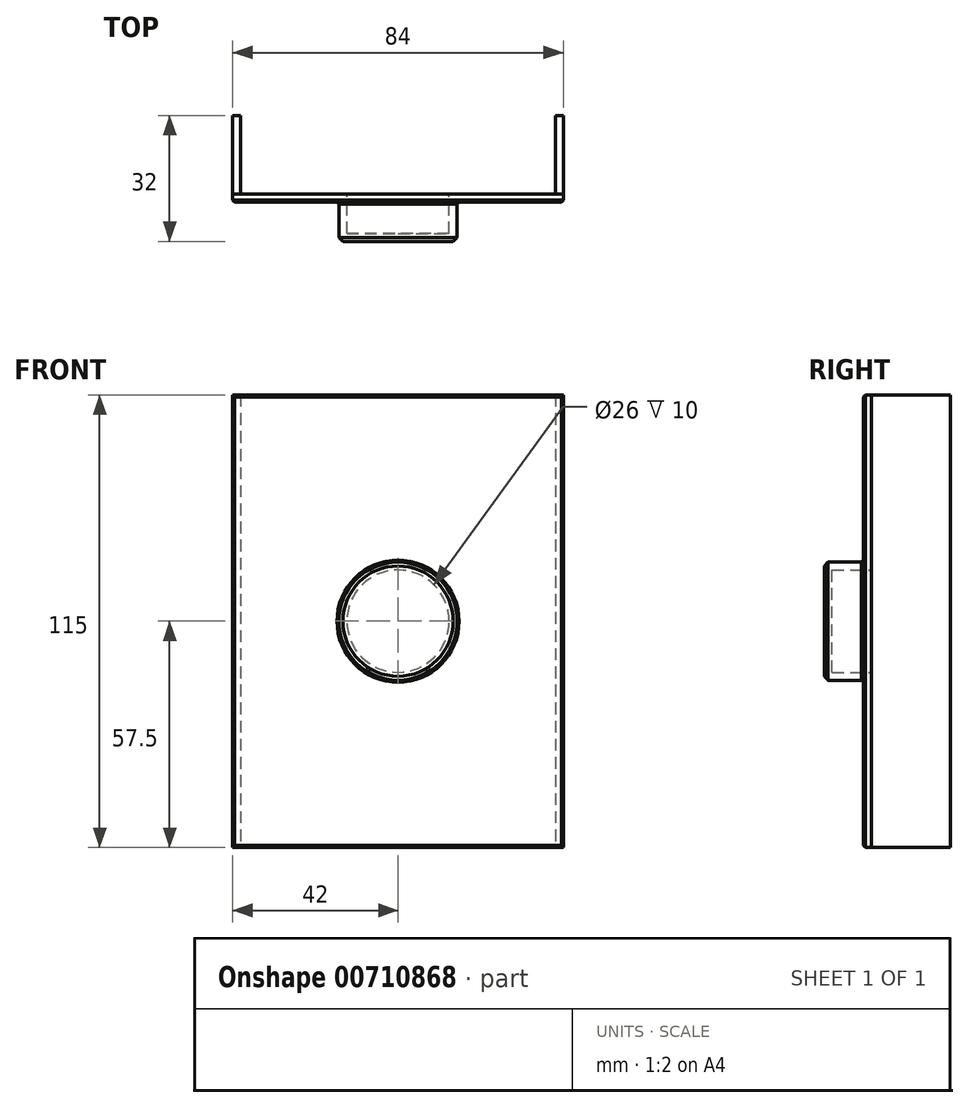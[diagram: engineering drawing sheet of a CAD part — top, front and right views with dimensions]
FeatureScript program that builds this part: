
annotation { "Feature Type Name" : "Feature", "Feature Type Description" : "" }
export const myFeature = defineFeature(function(context is Context, id is Id, definition is map)
    precondition{}
    {
        {
            var Q0;
            Q0=qCreatedBy(makeId("Front.planeOp"),FACE);
            var sketch = newSketch(context, id + "F0", { "sketchPlane" : qUnion([Q0])});
            skLineSegment(sketch, "E0.bottom", {"start": v(-40, 57.5) * mm, "end": v(40, 57.5) * mm});
            skLineSegment(sketch, "E0.top", {"start": v(-40, -57.5) * mm, "end": v(40, -57.5) * mm});
            skLineSegment(sketch, "E0.left", {"start": v(-40, 57.5) * mm, "end": v(-40, -57.5) * mm});
            skLineSegment(sketch, "E0.right", {"start": v(40, 57.5) * mm, "end": v(40, -57.5) * mm});
            skLineSegment(sketch, "E1.bottom", {"start": v(-40, 57.5) * mm, "end": v(-42, 57.5) * mm});
            skLineSegment(sketch, "E1.top", {"start": v(-40, -57.5) * mm, "end": v(-42, -57.5) * mm});
            skLineSegment(sketch, "E1.right", {"start": v(-42, 57.5) * mm, "end": v(-42, -57.5) * mm});
            skLineSegment(sketch, "E2.bottom", {"start": v(40, 57.5) * mm, "end": v(42, 57.5) * mm});
            skLineSegment(sketch, "E2.top", {"start": v(40, -57.5) * mm, "end": v(42, -57.5) * mm});
            skLineSegment(sketch, "E2.right", {"start": v(42, 57.5) * mm, "end": v(42, -57.5) * mm});
            skCircle(sketch, "E3", {"center": v(0, 0) * mm, "radius": 13 * mm});
            skCircle(sketch, "E4", {"center": v(0, 0) * mm, "radius": 15 * mm});
            skSolve(sketch);
        }
        {
            var Q0;
            Q0=makeQuery(id+"F0.imprint","IMPRINT",FACE,{"disambiguationData":[TD([[makeQuery(id+"F0.imprint","IMPRINT",EDGE,{"derivedFrom":sQuery(id+"F0.wireOp",EDGE,"E1.bottom")}),1.0]])]});
            extrude(context, id + "F1", {"entities" : qUnion([Q0]), "oppositeDirection" : true, "depth" : 20 * mm, "offsetDistance" : 25 * mm});
        }
        {
            var Q0;
            Q0=makeQuery(id+"F0.imprint","IMPRINT",FACE,{"disambiguationData":[TD([[makeQuery(id+"F0.imprint","IMPRINT",EDGE,{"derivedFrom":sQuery(id+"F0.wireOp",EDGE,"E2.bottom")}),-1.0]])]});
            extrude(context, id + "F2", {"entities" : qUnion([Q0]), "oppositeDirection" : true, "depth" : 20 * mm, "offsetDistance" : 25 * mm});
        }
        {
            var Q0;
            Q0=makeQuery(id+"F0.imprint","IMPRINT",FACE,{"disambiguationData":[TD([[makeQuery(id+"F0.imprint","IMPRINT",EDGE,{"derivedFrom":sQuery(id+"F0.wireOp",EDGE,"E0.bottom")}),-1.0]])]});
            var Q1;
            Q1=makeQuery(id+"F0.imprint","IMPRINT",FACE,{"disambiguationData":[TD([[makeQuery(id+"F0.imprint","IMPRINT",EDGE,{"derivedFrom":sQuery(id+"F0.wireOp",EDGE,"E2.bottom")}),-1.0]])]});
            var Q2;
            Q2=makeQuery(id+"F0.imprint","IMPRINT",FACE,{"disambiguationData":[TD([[makeQuery(id+"F0.imprint","IMPRINT",EDGE,{"derivedFrom":sQuery(id+"F0.wireOp",EDGE,"E1.bottom")}),1.0]])]});
            extrude(context, id + "F3", {"entities" : qUnion([Q0, Q1, Q2]), "depth" : 2 * mm, "offsetDistance" : 25 * mm});
        }
        {
            var Q0;
            Q0=makeQuery(id+"F0.imprint","IMPRINT",FACE,{"disambiguationData":[TD([[makeQuery(id+"F0.imprint","IMPRINT",EDGE,{"derivedFrom":sQuery(id+"F0.wireOp",EDGE,"E3")}),-1.0]])]});
            var Q1;
            Q1=makeQuery(id+"F0.imprint","IMPRINT",FACE,{"disambiguationData":[TD([[makeQuery(id+"F0.imprint","IMPRINT",EDGE,{"derivedFrom":sQuery(id+"F0.wireOp",EDGE,"E3")}),1.0]])]});
            extrude(context, id + "F4", {"entities" : qUnion([Q0, Q1]), "operationType" : NewBodyOperationType.ADD, "depth" : 12 * mm, "offsetDistance" : 25 * mm});
        }
        {
            var Q0;
            Q0=makeQuery(id+"F0.imprint","IMPRINT",FACE,{"disambiguationData":[TD([[makeQuery(id+"F0.imprint","IMPRINT",EDGE,{"derivedFrom":sQuery(id+"F0.wireOp",EDGE,"E3")}),1.0]])]});
            extrude(context, id + "F5", {"entities" : qUnion([Q0]), "operationType" : NewBodyOperationType.REMOVE, "depth" : 10 * mm, "offsetDistance" : 25 * mm});
        }
        {
            var Q0;
            Q0=makeQuery(id+"F3.opExtrude","CAP_FACE",FACE,{"disambiguationData":[OSD([sQuery(id+"F0.wireOp",EDGE,"E0.bottom"),sQuery(id+"F0.wireOp",EDGE,"E0.top"),sQuery(id+"F0.wireOp",EDGE,"E1.bottom"),sQuery(id+"F0.wireOp",EDGE,"E1.top"),sQuery(id+"F0.wireOp",EDGE,"E1.right"),sQuery(id+"F0.wireOp",EDGE,"E2.bottom"),sQuery(id+"F0.wireOp",EDGE,"E2.top"),sQuery(id+"F0.wireOp",EDGE,"E2.right"),sQuery(id+"F0.wireOp",EDGE,"E4")])],"isStart":false});
            chamfer(context, id + "F6", {"entities" : qUnion([Q0]), "width" : 0.5 * mm, "tangentPropagation" : true});
        }
        {
            var Q0;
            Q0=makeQuery(id+"F4.opExtrude","CAP_FACE",FACE,{"disambiguationData":[OSD([sQuery(id+"F0.wireOp",EDGE,"E4")])],"isStart":false});
            chamfer(context, id + "F7", {"entities" : qUnion([Q0]), "width" : 1 * mm, "tangentPropagation" : true});
        }
    });
